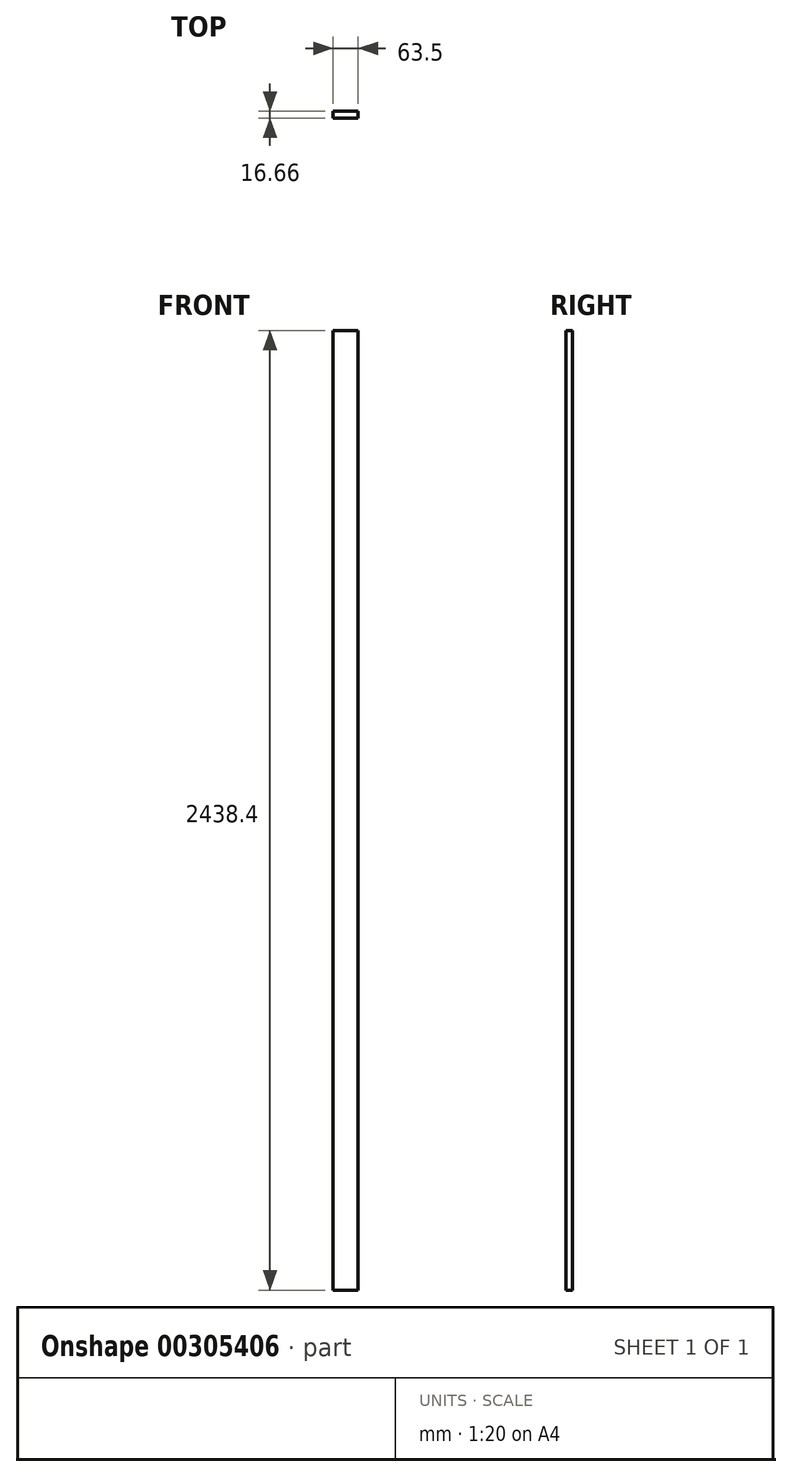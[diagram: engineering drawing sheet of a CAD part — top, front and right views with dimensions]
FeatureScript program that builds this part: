
annotation { "Feature Type Name" : "Feature", "Feature Type Description" : "" }
export const myFeature = defineFeature(function(context is Context, id is Id, definition is map)
    precondition{}
    {
        {
            var Q0;
            Q0=qCreatedBy(makeId("Front.planeOp"),FACE);
            var sketch = newSketch(context, id + "F0", { "sketchPlane" : qUnion([Q0])});
            skLineSegment(sketch, "E0.bottom", {"start": v(-33.23, 2235.19) * mm, "end": v(30.27, 2235.19) * mm});
            skLineSegment(sketch, "E0.top", {"start": v(-33.23, -203.21) * mm, "end": v(30.27, -203.21) * mm});
            skLineSegment(sketch, "E0.left", {"start": v(-33.23, 2235.19) * mm, "end": v(-33.23, -203.21) * mm});
            skLineSegment(sketch, "E0.right", {"start": v(30.27, 2235.19) * mm, "end": v(30.27, -203.21) * mm});
            skSolve(sketch);
        }
        {
            var Q0;
            Q0=makeQuery(id+"F0.imprint","IMPRINT",FACE,{"disambiguationData":[TD([[makeQuery(id+"F0.imprint","IMPRINT",EDGE,{"derivedFrom":sQuery(id+"F0.wireOp",EDGE,"E0.bottom")}),-1.0]])]});
            extrude(context, id + "F1", {"entities" : qUnion([Q0]), "depth" : 16.66 * mm});
        }
    });
